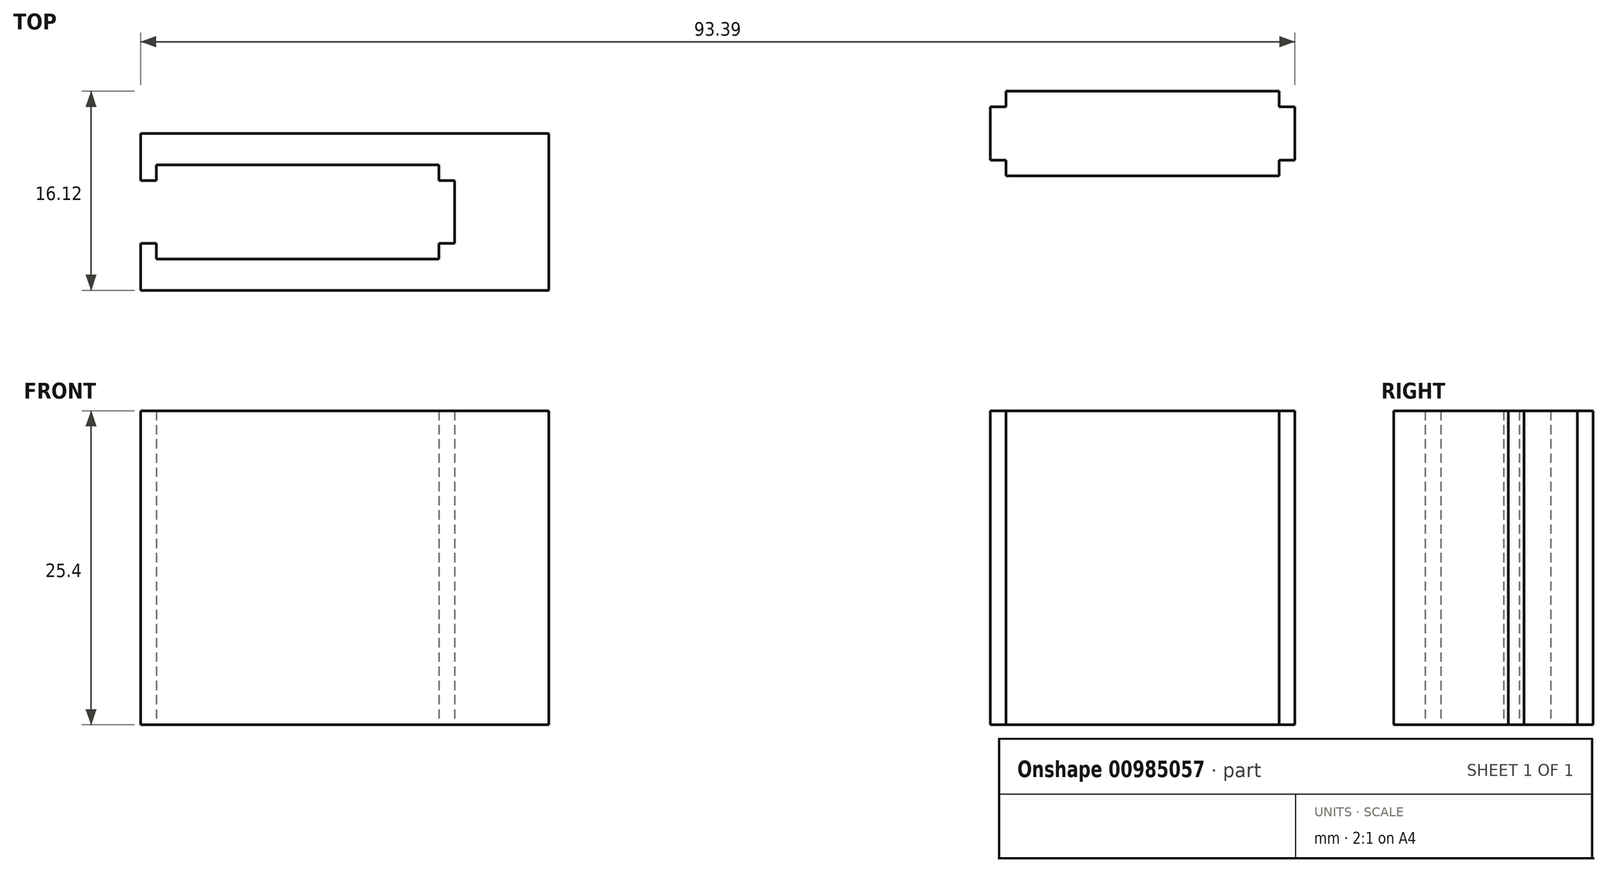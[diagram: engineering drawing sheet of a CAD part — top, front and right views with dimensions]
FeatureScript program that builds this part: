
annotation { "Feature Type Name" : "Feature", "Feature Type Description" : "" }
export const myFeature = defineFeature(function(context is Context, id is Id, definition is map)
    precondition{}
    {
        {
            var Q0;
            Q0=qCreatedBy(makeId("Top.planeOp"),FACE);
            var sketch = newSketch(context, id + "F0", { "sketchPlane" : qUnion([Q0])});
            skPoint(sketch, "E0.middle", {"position": v(0, 0) * mm});
            skLineSegment(sketch, "E1.bottom", {"start": v(-20.12, -2.59) * mm, "end": v(2.74, -2.59) * mm});
            skLineSegment(sketch, "E1.top", {"start": v(-20.12, -10.2) * mm, "end": v(2.74, -10.2) * mm});
            skLineSegment(sketch, "E1.left", {"start": v(-20.12, -2.59) * mm, "end": v(-20.12, -10.2) * mm});
            skLineSegment(sketch, "E1.right", {"start": v(2.74, -2.59) * mm, "end": v(2.74, -10.2) * mm});
            skLineSegment(sketch, "E2.bottom", {"start": v(-21.4, -3.86) * mm, "end": v(4, -3.86) * mm});
            skLineSegment(sketch, "E2.top", {"start": v(-21.4, -8.94) * mm, "end": v(4, -8.94) * mm});
            skLineSegment(sketch, "E2.left", {"start": v(-21.4, -3.86) * mm, "end": v(-21.4, -8.94) * mm});
            skLineSegment(sketch, "E2.right", {"start": v(4, -3.86) * mm, "end": v(4, -8.94) * mm});
            skLineSegment(sketch, "E3.bottom", {"start": v(-21.4, -0.05) * mm, "end": v(11.63, -0.05) * mm});
            skLineSegment(sketch, "E3.top", {"start": v(-21.4, -12.75) * mm, "end": v(11.63, -12.75) * mm});
            skLineSegment(sketch, "E3.left", {"start": v(-21.4, -0.05) * mm, "end": v(-21.4, -12.75) * mm});
            skLineSegment(sketch, "E3.right", {"start": v(11.63, -0.05) * mm, "end": v(11.63, -12.75) * mm});
            skLineSegment(sketch, "E4.bottom", {"start": v(47.36, 2.1) * mm, "end": v(72, 2.1) * mm});
            skLineSegment(sketch, "E4.top", {"start": v(47.36, -2.22) * mm, "end": v(72, -2.22) * mm});
            skLineSegment(sketch, "E4.left", {"start": v(47.36, 2.1) * mm, "end": v(47.36, -2.22) * mm});
            skLineSegment(sketch, "E4.right", {"start": v(72, 2.1) * mm, "end": v(72, -2.22) * mm});
            skLineSegment(sketch, "E5.bottom", {"start": v(48.63, 3.37) * mm, "end": v(70.73, 3.37) * mm});
            skLineSegment(sketch, "E5.top", {"start": v(48.63, -3.5) * mm, "end": v(70.73, -3.5) * mm});
            skLineSegment(sketch, "E5.left", {"start": v(48.63, 3.37) * mm, "end": v(48.63, -3.5) * mm});
            skLineSegment(sketch, "E5.right", {"start": v(70.73, 3.37) * mm, "end": v(70.73, -3.5) * mm});
            skSolve(sketch);
        }
        {
            var Q0;
            {var subQ10=sQuery(id+"F0.wireOp",EDGE,"9KUCF74i-xbnd-lc6K-Wayc-NxSG1CZFUXqN.bottom");Q0=makeQuery(id+"F0.imprint","IMPRINT",FACE,{"disambiguationData":[TD([[makeQuery(id+"F0.imprint","IMPRINT",EDGE,{"derivedFrom":subQ10}),-1.0]])]});}
            var Q1;
            {var subQ0=sQuery(id+"F0.wireOp",EDGE,"gmHeMQLf-frzd-8Fp1-iP4Q-3Oatf1pchCuO.bottom");Q1=makeQuery(id+"F0.imprint","IMPRINT",FACE,{"disambiguationData":[TD([[makeQuery(id+"F0.imprint","IMPRINT",EDGE,{"derivedFrom":subQ0}),-1.0]])]});}
            var Q2;
            {var subQ0=sQuery(id+"F0.wireOp",EDGE,"E5IvgVDQ-jky9-ToZX-P9Xx-3ixWtNsdH63Z.bottom");var subQ1=sQuery(id+"F0.wireOp",EDGE,"gmHeMQLf-frzd-8Fp1-iP4Q-3Oatf1pchCuO.left");var subQ2=makeQuery(id+"F0.imprint","INTERSECT",VERTEX,{"derivedFrom":[subQ1,subQ0]});Q2=makeQuery(id+"F0.imprint","IMPRINT",FACE,{"disambiguationData":[TD([[makeQuery(id+"F0.imprint","IMPRINT",EDGE,{"disambiguationData":[TD([[subQ2,-1.0]])],"derivedFrom":subQ1}),1.0]])]});}
            var Q3;
            {var subQ0=sQuery(id+"F0.wireOp",EDGE,"gmHeMQLf-frzd-8Fp1-iP4Q-3Oatf1pchCuO.top");Q3=makeQuery(id+"F0.imprint","IMPRINT",FACE,{"disambiguationData":[TD([[makeQuery(id+"F0.imprint","IMPRINT",EDGE,{"derivedFrom":subQ0}),1.0]])]});}
            var Q4;
            {var subQ5=sQuery(id+"F0.wireOp",EDGE,"E5IvgVDQ-jky9-ToZX-P9Xx-3ixWtNsdH63Z.left");Q4=makeQuery(id+"F0.imprint","IMPRINT",FACE,{"disambiguationData":[TD([[makeQuery(id+"F0.imprint","IMPRINT",EDGE,{"derivedFrom":subQ5}),1.0]])]});}
            var Q5;
            {var subQ5=sQuery(id+"F0.wireOp",EDGE,"E5IvgVDQ-jky9-ToZX-P9Xx-3ixWtNsdH63Z.right");Q5=makeQuery(id+"F0.imprint","IMPRINT",FACE,{"disambiguationData":[TD([[makeQuery(id+"F0.imprint","IMPRINT",EDGE,{"derivedFrom":subQ5}),-1.0]])]});}
            var Q6;
            {var subQ11=sQuery(id+"F0.wireOp",EDGE,"E1.bottom");Q6=makeQuery(id+"F0.imprint","IMPRINT",FACE,{"disambiguationData":[TD([[makeQuery(id+"F0.imprint","IMPRINT",EDGE,{"derivedFrom":subQ11}),1.0]])]});}
            var Q7;
            {var subQ0=sQuery(id+"F0.wireOp",EDGE,"E5.left");var subQ1=sQuery(id+"F0.wireOp",EDGE,"E4.bottom");var subQ2=makeQuery(id+"F0.imprint","INTERSECT",VERTEX,{"derivedFrom":[subQ1,subQ0]});Q7=makeQuery(id+"F0.imprint","IMPRINT",FACE,{"disambiguationData":[TD([[makeQuery(id+"F0.imprint","IMPRINT",EDGE,{"disambiguationData":[TD([[subQ2,-1.0]])],"derivedFrom":subQ1}),-1.0]])]});}
            var Q8;
            {var subQ0=sQuery(id+"F0.wireOp",EDGE,"E4.left");Q8=makeQuery(id+"F0.imprint","IMPRINT",FACE,{"disambiguationData":[TD([[makeQuery(id+"F0.imprint","IMPRINT",EDGE,{"derivedFrom":subQ0}),1.0]])]});}
            var Q9;
            {var subQ5=sQuery(id+"F0.wireOp",EDGE,"E5.top");Q9=makeQuery(id+"F0.imprint","IMPRINT",FACE,{"disambiguationData":[TD([[makeQuery(id+"F0.imprint","IMPRINT",EDGE,{"derivedFrom":subQ5}),1.0]])]});}
            var Q10;
            {var subQ5=sQuery(id+"F0.wireOp",EDGE,"E5.bottom");Q10=makeQuery(id+"F0.imprint","IMPRINT",FACE,{"disambiguationData":[TD([[makeQuery(id+"F0.imprint","IMPRINT",EDGE,{"derivedFrom":subQ5}),-1.0]])]});}
            var Q11;
            {var subQ0=sQuery(id+"F0.wireOp",EDGE,"E4.right");Q11=makeQuery(id+"F0.imprint","IMPRINT",FACE,{"disambiguationData":[TD([[makeQuery(id+"F0.imprint","IMPRINT",EDGE,{"derivedFrom":subQ0}),-1.0]])]});}
            extrude(context, id + "F1", {"entities" : qUnion([Q0, Q1, Q2, Q3, Q4, Q5, Q6, Q7, Q8, Q9, Q10, Q11]), "depth" : 25.4 * mm, "offsetDistance" : 25.4 * mm});
        }
    });
